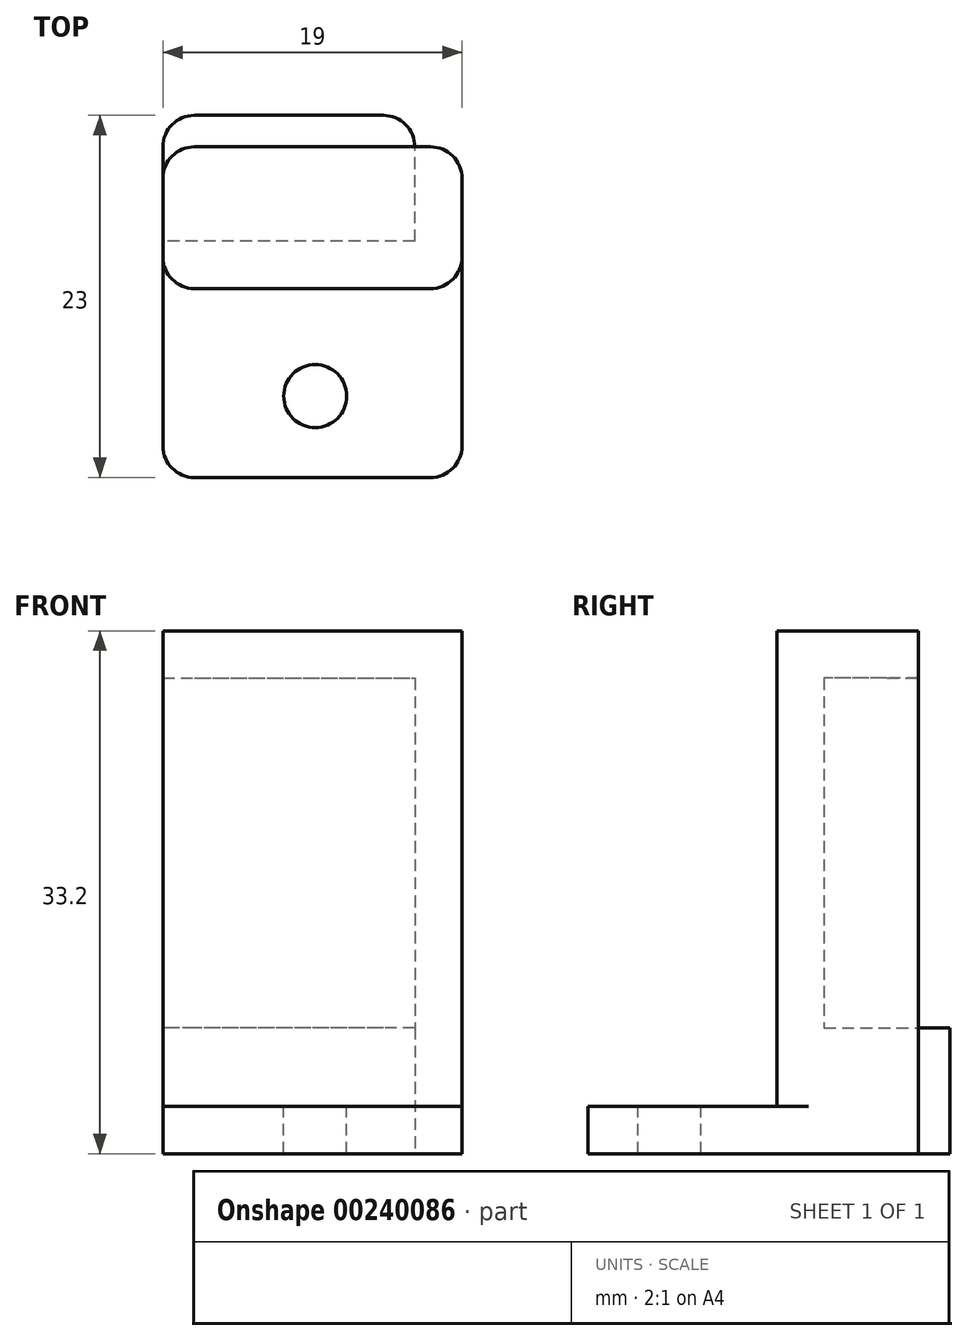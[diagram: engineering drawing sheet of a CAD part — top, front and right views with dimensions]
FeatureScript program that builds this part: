
annotation { "Feature Type Name" : "Feature", "Feature Type Description" : "" }
export const myFeature = defineFeature(function(context is Context, id is Id, definition is map)
    precondition{}
    {
        {
            var Q0;
            Q0=qCreatedBy(makeId("Top.planeOp"),FACE);
            var sketch = newSketch(context, id + "F0", { "sketchPlane" : qUnion([Q0])});
            skLineSegment(sketch, "E0", {"start": v(-69.9, 0) * mm, "end": v(79.98, 0) * mm, "construction": true});
            skLineSegment(sketch, "E1", {"start": v(0, 59.98) * mm, "end": v(0, -61.02) * mm, "construction": true});
            skLineSegment(sketch, "E2.bottom", {"start": v(0, 0) * mm, "end": v(-16, 0) * mm});
            skLineSegment(sketch, "E2.top", {"start": v(0, 8) * mm, "end": v(-16, 8) * mm});
            skLineSegment(sketch, "E2.left", {"start": v(0, 0) * mm, "end": v(0, 8) * mm});
            skLineSegment(sketch, "E2.right", {"start": v(-16, 0) * mm, "end": v(-16, 8) * mm});
            skSolve(sketch);
        }
        {
            var Q0;
            Q0 = qSketchRegion(id + "F0", true);
            extrude(context, id + "F1", {"entities" : qUnion([Q0]), "depth" : 8 * mm});
        }
        {
            var Q0;
            Q0=qCreatedBy(makeId("Top.planeOp"),FACE);
            var sketch = newSketch(context, id + "F2", { "sketchPlane" : qUnion([Q0])});
            skLineSegment(sketch, "E3.bottom", {"start": v(0, 0) * mm, "end": v(-16, 0) * mm});
            skLineSegment(sketch, "E3.top", {"start": v(0, -3) * mm, "end": v(-16, -3) * mm});
            skLineSegment(sketch, "E3.left", {"start": v(0, 0) * mm, "end": v(0, -3) * mm});
            skLineSegment(sketch, "E3.right", {"start": v(-16, 0) * mm, "end": v(-16, -3) * mm});
            skLineSegment(sketch, "E4.bottom", {"start": v(0, -3) * mm, "end": v(3, -3) * mm});
            skLineSegment(sketch, "E4.top", {"start": v(0, 6) * mm, "end": v(3, 6) * mm});
            skLineSegment(sketch, "E4.left", {"start": v(0, -3) * mm, "end": v(0, 6) * mm});
            skLineSegment(sketch, "E4.right", {"start": v(3, -3) * mm, "end": v(3, 6) * mm});
            skSolve(sketch);
        }
        {
            var Q0;
            Q0 = qSketchRegion(id + "F2", true);
            extrude(context, id + "F3", {"entities" : qUnion([Q0]), "operationType" : NewBodyOperationType.ADD, "depth" : 33.2 * mm});
        }
        {
            var Q0;
            Q0=makeQuery(id+"F3.opExtrude","SWEPT_FACE",FACE,{"disambiguationData":[OSD([sQuery(id+"F2.wireOp",EDGE,"E3.top"),sQuery(id+"F2.wireOp",EDGE,"E4.bottom")])]});
            var sketch = newSketch(context, id + "F4", { "sketchPlane" : qUnion([Q0])});
            skLineSegment(sketch, "E5.bottom", {"start": v(-16, 0) * mm, "end": v(3, 0) * mm});
            skLineSegment(sketch, "E5.top", {"start": v(-16, 3) * mm, "end": v(3, 3) * mm});
            skLineSegment(sketch, "E5.left", {"start": v(-16, 0) * mm, "end": v(-16, 3) * mm});
            skLineSegment(sketch, "E5.right", {"start": v(3, 0) * mm, "end": v(3, 3) * mm});
            skSolve(sketch);
        }
        {
            var Q0;
            Q0 = qSketchRegion(id + "F4", true);
            extrude(context, id + "F5", {"entities" : qUnion([Q0]), "operationType" : NewBodyOperationType.ADD, "depth" : 12 * mm});
        }
        {
            var Q0;
            Q0=makeQuery(id+"F5.opExtrude","SWEPT_FACE",FACE,{"disambiguationData":[OSD([sQuery(id+"F4.wireOp",EDGE,"E5.top")])]});
            var sketch = newSketch(context, id + "F6", { "sketchPlane" : qUnion([Q0])});
            skCircle(sketch, "E6", {"center": v(-6.32, -9.83) * mm, "radius": 2 * mm});
            skSolve(sketch);
        }
        {
            var Q0;
            Q0 = qSketchRegion(id + "F6", true);
            var Q1;
            Q1=makeQuery(id+"F5.boolean.opBoolean","MERGE",FACE,{"derivedFrom":[makeQuery(id+"F3.boolean.opBoolean","MERGE",FACE,{"derivedFrom":[makeQuery(id+"F1.opExtrude","CAP_FACE",FACE,{"disambiguationData":[OSD([sQuery(id+"F0.wireOp",EDGE,"E2.bottom"),sQuery(id+"F0.wireOp",EDGE,"E2.top"),sQuery(id+"F0.wireOp",EDGE,"E2.left"),sQuery(id+"F0.wireOp",EDGE,"E2.right")])],"isStart":true}),makeQuery(id+"F3.opExtrude","CAP_FACE",FACE,{"disambiguationData":[OSD([sQuery(id+"F2.wireOp",EDGE,"E3.bottom"),sQuery(id+"F2.wireOp",EDGE,"E3.top"),sQuery(id+"F2.wireOp",EDGE,"E3.right"),sQuery(id+"F2.wireOp",EDGE,"E4.bottom"),sQuery(id+"F2.wireOp",EDGE,"E4.top"),sQuery(id+"F2.wireOp",EDGE,"E4.left"),sQuery(id+"F2.wireOp",EDGE,"E4.right")])],"isStart":true})]}),makeQuery(id+"F5.opExtrude","SWEPT_FACE",FACE,{"disambiguationData":[OSD([sQuery(id+"F4.wireOp",EDGE,"E5.bottom")])]})]});
            extrude(context, id + "F7", {"entities" : qUnion([Q0]), "operationType" : NewBodyOperationType.REMOVE, "endBound" : BoundingType.UP_TO_SURFACE, "oppositeDirection" : true, "endBoundEntityFace" : qUnion([Q1]), "depth" : 25 * mm});
        }
        {
            var Q0;
            Q0=makeQuery(id+"F3.opExtrude","SWEPT_FACE",FACE,{"disambiguationData":[OSD([sQuery(id+"F2.wireOp",EDGE,"E3.bottom")])]});
            var sketch = newSketch(context, id + "F8", { "sketchPlane" : qUnion([Q0])});
            skLineSegment(sketch, "E7.bottom", {"start": v(16, 33.2) * mm, "end": v(0, 33.2) * mm});
            skLineSegment(sketch, "E7.top", {"start": v(16, 30.2) * mm, "end": v(0, 30.2) * mm});
            skLineSegment(sketch, "E7.left", {"start": v(16, 33.2) * mm, "end": v(16, 30.2) * mm});
            skLineSegment(sketch, "E7.right", {"start": v(0, 33.2) * mm, "end": v(0, 30.2) * mm});
            skSolve(sketch);
        }
        {
            var Q0;
            Q0 = qSketchRegion(id + "F8", true);
            extrude(context, id + "F9", {"entities" : qUnion([Q0]), "operationType" : NewBodyOperationType.ADD, "depth" : 6 * mm});
        }
        {
            var Q0;
            Q0=makeQuery(id+"F9.opExtrude","CAP_EDGE",EDGE,{"disambiguationData":[OSD([sQuery(id+"F8.wireOp",EDGE,"E7.left")])],"isStart":false});
            var Q1;
            Q1=makeQuery(id+"F1.opExtrude","SWEPT_EDGE",EDGE,{"disambiguationData":[OSD([sQuery(id+"F0.wireOp",EDGE,"E2.top"),sQuery(id+"F0.wireOp",EDGE,"E2.right")])]});
            var Q2;
            Q2=makeQuery(id+"F1.opExtrude","SWEPT_EDGE",EDGE,{"disambiguationData":[OSD([sQuery(id+"F0.wireOp",EDGE,"E2.top"),sQuery(id+"F0.wireOp",EDGE,"E2.left")])]});
            var Q3;
            Q3=makeQuery(id+"F3.opExtrude","SWEPT_EDGE",EDGE,{"disambiguationData":[OSD([sQuery(id+"F2.wireOp",EDGE,"E4.top"),sQuery(id+"F2.wireOp",EDGE,"E4.right")])]});
            var Q4;
            Q4=makeQuery(id+"F5.opExtrude","CAP_EDGE",EDGE,{"disambiguationData":[OSD([sQuery(id+"F4.wireOp",EDGE,"E5.right")])],"isStart":false});
            var Q5;
            Q5=makeQuery(id+"F3.opExtrude","SWEPT_EDGE",EDGE,{"disambiguationData":[OSD([sQuery(id+"F2.wireOp",EDGE,"E4.bottom"),sQuery(id+"F2.wireOp",EDGE,"E4.right")])]});
            var Q6;
            Q6=makeQuery(id+"F3.opExtrude","SWEPT_EDGE",EDGE,{"disambiguationData":[OSD([sQuery(id+"F2.wireOp",EDGE,"E3.top"),sQuery(id+"F2.wireOp",EDGE,"E3.right")])]});
            var Q7;
            Q7=makeQuery(id+"F5.opExtrude","CAP_EDGE",EDGE,{"disambiguationData":[OSD([sQuery(id+"F4.wireOp",EDGE,"E5.left")])],"isStart":false});
            fillet(context, id + "F10", {"entities" : qUnion([Q0, Q1, Q2, Q3, Q4, Q5, Q6, Q7]), "radius" : 2 * mm, "tangentPropagation" : true, "allowEdgeOverflow" : false});
        }
    });
